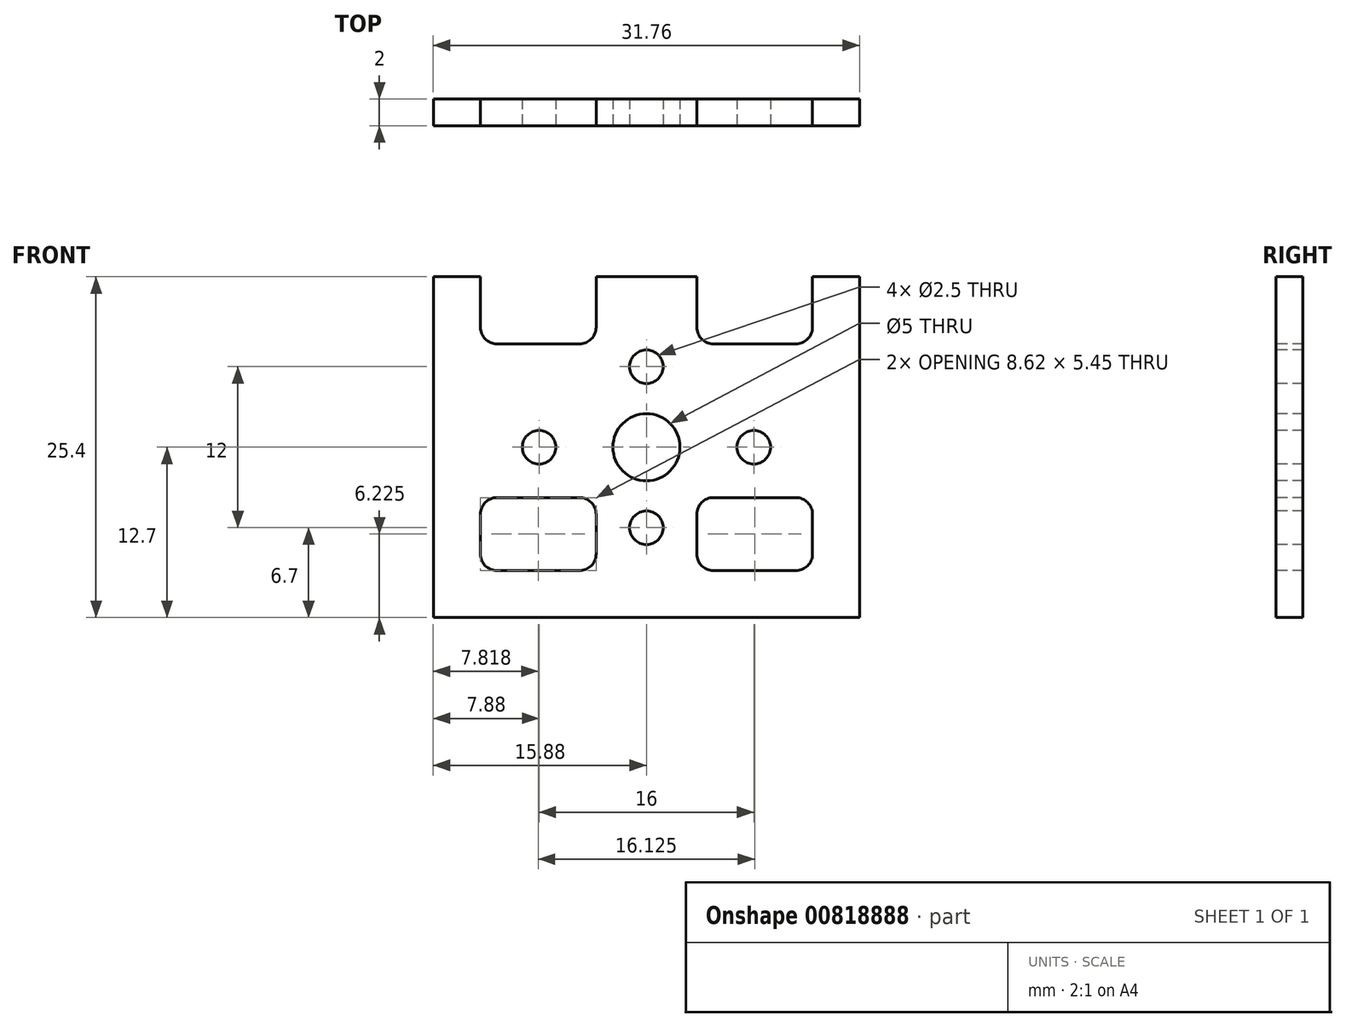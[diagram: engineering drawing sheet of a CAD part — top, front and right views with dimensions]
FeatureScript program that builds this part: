
annotation { "Feature Type Name" : "Feature", "Feature Type Description" : "" }
export const myFeature = defineFeature(function(context is Context, id is Id, definition is map)
    precondition{}
    {
        {
            assignVariable(context, id + "F0", {"name" : "firewall_thickness_mm", "anyValue" : 2});
        }
        {
            var Q0;
            Q0=qCreatedBy(makeId("Front.planeOp"),FACE);
            var sketch = newSketch(context, id + "F1", { "sketchPlane" : qUnion([Q0])});
            skLineSegment(sketch, "E0.bottom", {"start": v(15.88, 12.7) * mm, "end": v(-15.88, 12.7) * mm});
            skLineSegment(sketch, "E0.top", {"start": v(15.88, -12.7) * mm, "end": v(-15.88, -12.7) * mm});
            skLineSegment(sketch, "E0.left", {"start": v(15.88, 12.7) * mm, "end": v(15.87, -12.7) * mm});
            skLineSegment(sketch, "E0.right", {"start": v(-15.88, 12.7) * mm, "end": v(-15.88, -12.7) * mm});
            skPoint(sketch, "E0.middle", {"position": v(0, 0) * mm});
            skSolve(sketch);
        }
        {
            var Q0;
            Q0=qSketchRegion(id+"F1",true);
            extrude(context, id + "F2", {"entities" : qUnion([Q0]), "oppositeDirection" : true, "depth" : (getVariable(context, 'firewall_thickness_mm')) * mm, "offsetDistance" : 25 * mm});
        }
        {
            var Q0;
            Q0=makeQuery(id+"F1.imprint","IMPRINT",FACE,{"disambiguationData":[TD([[makeQuery(id+"F1.imprint","IMPRINT",EDGE,{"derivedFrom":sQuery(id+"F1.wireOp",EDGE,"E0.bottom")}),1.0]])]});
            var sketch = newSketch(context, id + "F3", { "sketchPlane" : qUnion([Q0])});
            skCircle(sketch, "E1", {"center": v(0, 0) * mm, "radius": 2.5 * mm});
            skCircle(sketch, "E2", {"center": v(-8, 0) * mm, "radius": 1.25 * mm});
            skCircle(sketch, "E3.MirrorC", {"center": v(8, 0) * mm, "radius": 1.25 * mm});
            skCircle(sketch, "E4", {"center": v(0, 6) * mm, "radius": 1.25 * mm});
            skLineSegment(sketch, "E5", {"start": v(-15.88, 0) * mm, "end": v(15.88, 0) * mm, "construction": true});
            skLineSegment(sketch, "E6", {"start": v(0, 12.7) * mm, "end": v(0, -12.7) * mm, "construction": true});
            skCircle(sketch, "E7.MirrorC", {"center": v(0, -6) * mm, "radius": 1.25 * mm});
            skSolve(sketch);
        }
        {
            var Q0;
            Q0=makeQuery(id+"F1.imprint","IMPRINT",FACE,{"disambiguationData":[TD([[makeQuery(id+"F1.imprint","IMPRINT",EDGE,{"derivedFrom":sQuery(id+"F1.wireOp",EDGE,"E0.bottom")}),1.0]])]});
            var sketch = newSketch(context, id + "F4", { "sketchPlane" : qUnion([Q0])});
            skLineSegment(sketch, "E8.bottom", {"start": v(-14.88, -1.25) * mm, "end": v(-1.25, -1.25) * mm, "construction": true});
            skLineSegment(sketch, "E8.top", {"start": v(-14.88, -11.7) * mm, "end": v(-1.25, -11.7) * mm, "construction": true});
            skLineSegment(sketch, "E8.left", {"start": v(-14.88, -1.25) * mm, "end": v(-14.88, -11.7) * mm, "construction": true});
            skLineSegment(sketch, "E8.right", {"start": v(-1.25, -1.25) * mm, "end": v(-1.25, -11.7) * mm, "construction": true});
            skLineSegment(sketch, "E9.0", {"start": v(-3.75, -5) * mm, "end": v(-3.75, -7.95) * mm});
            skLineSegment(sketch, "E9.1", {"start": v(-11.13, -3.75) * mm, "end": v(-5, -3.75) * mm});
            skLineSegment(sketch, "E9.2", {"start": v(-12.38, -5) * mm, "end": v(-12.38, -7.95) * mm});
            skLineSegment(sketch, "E9.3", {"start": v(-11.13, -9.2) * mm, "end": v(-5, -9.2) * mm});
            skPoint(sketch, "E10.visualSharp", {"position": v(-12.38, -3.75) * mm});
            skArc(sketch, "E10.filletArc", {"start": v(-11.13, -3.75) * mm, "mid": v(-12, -4.12) * mm, "end": v(-12.38, -5) * mm});
            skPoint(sketch, "E11.visualSharp", {"position": v(-3.75, -3.75) * mm});
            skArc(sketch, "E11.filletArc", {"start": v(-3.75, -5) * mm, "mid": v(-4.12, -4.12) * mm, "end": v(-5, -3.75) * mm});
            skPoint(sketch, "E12.visualSharp", {"position": v(-3.75, -9.2) * mm});
            skArc(sketch, "E12.filletArc", {"start": v(-5, -9.2) * mm, "mid": v(-4.12, -8.83) * mm, "end": v(-3.75, -7.95) * mm});
            skPoint(sketch, "E13.visualSharp", {"position": v(-12.38, -9.2) * mm});
            skArc(sketch, "E13.filletArc", {"start": v(-12.38, -7.95) * mm, "mid": v(-12, -8.83) * mm, "end": v(-11.13, -9.2) * mm});
            skArc(sketch, "E14.MirrorCS", {"start": v(3.75, -5) * mm, "mid": v(4.12, -4.12) * mm, "end": v(5, -3.75) * mm});
            skLineSegment(sketch, "E15.MirrorCS", {"start": v(11.13, -3.75) * mm, "end": v(5, -3.75) * mm});
            skArc(sketch, "E16.MirrorCS", {"start": v(11.13, -3.75) * mm, "mid": v(12, -4.12) * mm, "end": v(12.38, -5) * mm});
            skLineSegment(sketch, "E17.MirrorCS", {"start": v(12.38, -5) * mm, "end": v(12.38, -7.95) * mm});
            skArc(sketch, "E18.MirrorCS", {"start": v(12.38, -7.95) * mm, "mid": v(12, -8.83) * mm, "end": v(11.13, -9.2) * mm});
            skLineSegment(sketch, "E19.MirrorCS", {"start": v(11.13, -9.2) * mm, "end": v(5, -9.2) * mm});
            skArc(sketch, "E20.MirrorCS", {"start": v(5, -9.2) * mm, "mid": v(4.12, -8.83) * mm, "end": v(3.75, -7.95) * mm});
            skLineSegment(sketch, "E21.MirrorCS", {"start": v(3.75, -5) * mm, "end": v(3.75, -7.95) * mm});
            skLineSegment(sketch, "E22", {"start": v(-12.38, 12.7) * mm, "end": v(-12.38, 8.95) * mm});
            skLineSegment(sketch, "E23", {"start": v(-3.75, 8.95) * mm, "end": v(-3.75, 12.7) * mm});
            skLineSegment(sketch, "E24", {"start": v(-11.13, 7.7) * mm, "end": v(-5, 7.7) * mm});
            skPoint(sketch, "E25.visualSharp", {"position": v(-12.38, 7.7) * mm});
            skArc(sketch, "E25.filletArc", {"start": v(-12.38, 8.95) * mm, "mid": v(-12, 8.07) * mm, "end": v(-11.13, 7.7) * mm});
            skPoint(sketch, "E26.visualSharp", {"position": v(-3.75, 7.7) * mm});
            skArc(sketch, "E26.filletArc", {"start": v(-5, 7.7) * mm, "mid": v(-4.12, 8.07) * mm, "end": v(-3.75, 8.95) * mm});
            skLineSegment(sketch, "E27.MirrorCS", {"start": v(3.75, 8.95) * mm, "end": v(3.75, 12.7) * mm});
            skArc(sketch, "E28.MirrorCS", {"start": v(5, 7.7) * mm, "mid": v(4.12, 8.07) * mm, "end": v(3.75, 8.95) * mm});
            skLineSegment(sketch, "E29.MirrorCS", {"start": v(11.13, 7.7) * mm, "end": v(5, 7.7) * mm});
            skArc(sketch, "E30.MirrorCS", {"start": v(12.38, 8.95) * mm, "mid": v(12, 8.07) * mm, "end": v(11.13, 7.7) * mm});
            skLineSegment(sketch, "E31.MirrorCS", {"start": v(12.38, 12.7) * mm, "end": v(12.38, 8.95) * mm});
            skLineSegment(sketch, "E32", {"start": v(-12.38, 12.7) * mm, "end": v(-3.75, 12.7) * mm});
            skLineSegment(sketch, "E33.MirrorCS", {"start": v(12.38, 12.7) * mm, "end": v(3.75, 12.7) * mm});
            skLineSegment(sketch, "E34.0", {"start": v(-15.88, -12.7) * mm, "end": v(0, -12.7) * mm});
            skLineSegment(sketch, "E34.1", {"start": v(-15.88, 0) * mm, "end": v(-15.88, -12.7) * mm});
            skSolve(sketch);
        }
        {
            var Q0;
            Q0=qSketchRegion(id+"F3",true);
            var Q1;
            Q1=qSketchRegion(id+"F4",true);
            extrude(context, id + "F5", {"entities" : qUnion([Q0, Q1]), "operationType" : NewBodyOperationType.REMOVE, "endBound" : BoundingType.THROUGH_ALL, "oppositeDirection" : true, "depth" : 25 * mm, "offsetDistance" : 25 * mm});
        }
    });
